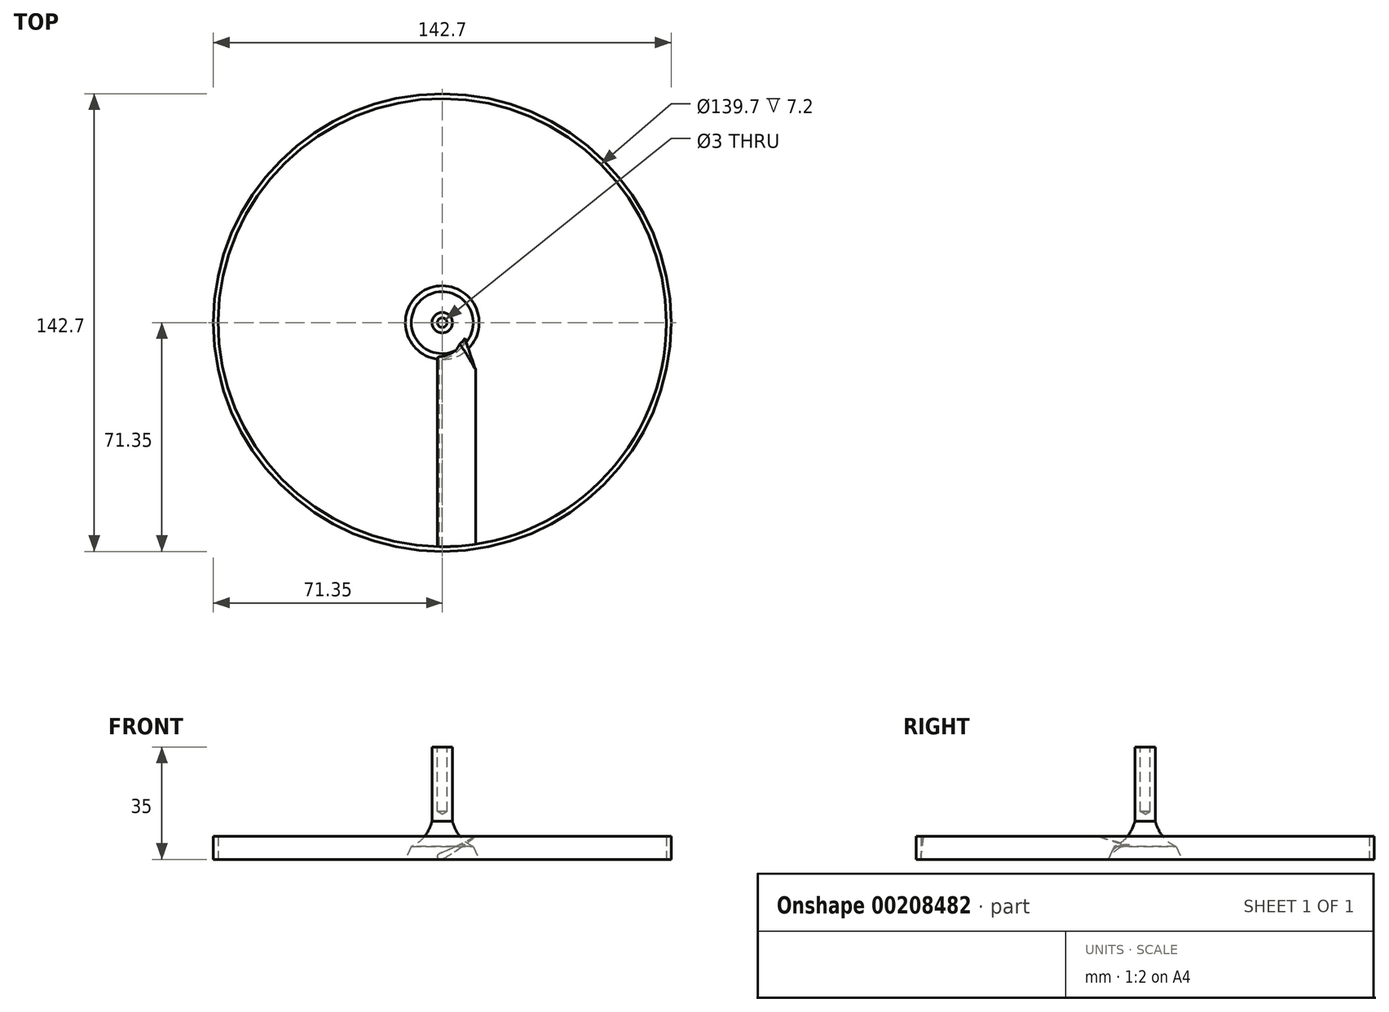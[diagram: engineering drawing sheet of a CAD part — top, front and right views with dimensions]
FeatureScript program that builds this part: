
annotation { "Feature Type Name" : "Feature", "Feature Type Description" : "" }
export const myFeature = defineFeature(function(context is Context, id is Id, definition is map)
    precondition{}
    {
        {
            var Q0;
            Q0=qCreatedBy(makeId("Front.planeOp"),FACE);
            var sketch = newSketch(context, id + "F0", { "sketchPlane" : qUnion([Q0])});
            skLineSegment(sketch, "E0", {"start": v(0, 0) * mm, "end": v(11, 6.35) * mm, "construction": true});
            skLineSegment(sketch, "E1", {"start": v(0, 0) * mm, "end": v(3.86, 0) * mm, "construction": true});
            skLineSegment(sketch, "E2.0", {"start": v(-0.62, 0.8) * mm, "end": v(10.38, 7.14) * mm, "construction": true});
            skFitSpline(sketch, "E3", {"points": [v(0, 0) * mm, v(2.62, 1.51) * mm, v(7.27, 4.68) * mm, v(10.38, 7.14) * mm], "startDerivative": vector(8.9, 4.4) * mm, "endDerivative": vector(8.82, 7.21) * mm});
            skLineSegment(sketch, "E4.0", {"start": v(-0.75, 1.88) * mm, "end": v(9.88, 8.01) * mm, "construction": true});
            skFitSpline(sketch, "E5", {"points": [v(-0.75, 1.88) * mm, v(2.33, 3.15) * mm, v(6.1, 4.85) * mm, v(10.38, 7.14) * mm], "startDerivative": vector(11.35, 3.56) * mm, "endDerivative": vector(12.14, 6.7) * mm});
            skArc(sketch, "E6", {"start": v(-0.75, 1.88) * mm, "mid": v(-1.39, 0.53) * mm, "end": v(0, 0) * mm});
            skLineSegment(sketch, "E7", {"start": v(0, 0) * mm, "end": v(0, 29.65) * mm, "construction": true});
            skSolve(sketch);
        }
        {
            var Q0;
            Q0 = qSketchRegion(id + "F0", true);
            extrude(context, id + "F1", {"entities" : qUnion([Q0]), "depth" : 69.85 * mm});
        }
        {
            var Q0;
            Q0=qCreatedBy(makeId("Front.planeOp"),FACE);
            var sketch = newSketch(context, id + "F2", { "sketchPlane" : qUnion([Q0])});
            skLineSegment(sketch, "E8", {"start": v(0, 2.13) * mm, "end": v(20.26, 7.8) * mm});
            skLineSegment(sketch, "E9", {"start": v(20.26, 7.8) * mm, "end": v(0, 7.8) * mm});
            skLineSegment(sketch, "E10", {"start": v(0, 7.8) * mm, "end": v(0, 2.13) * mm});
            skSolve(sketch);
        }
        {
            var Q0;
            Q0 = qSketchRegion(id + "F2", true);
            var Q1;
            Q1=sQuery(id+"F0.wireOp",EDGE,"E7");
            revolve(context, id + "F3", {"operationType" : NewBodyOperationType.REMOVE, "entities" : qUnion([Q0]), "axis" : qUnion([Q1]), "revolveType" : RevolveType.FULL, "oppositeDirection" : true});
        }
        {
            var Q0;
            Q0=qCreatedBy(makeId("Top.planeOp"),FACE);
            var sketch = newSketch(context, id + "F4", { "sketchPlane" : qUnion([Q0])});
            skCircle(sketch, "E11", {"center": v(0, 0) * mm, "radius": 3.18 * mm});
            skSolve(sketch);
        }
        {
            var Q0;
            Q0 = qSketchRegion(id + "F4", true);
            extrude(context, id + "F5", {"entities" : qUnion([Q0]), "operationType" : NewBodyOperationType.ADD, "depth" : 35 * mm});
        }
        {
            var Q0;
            Q0=qCreatedBy(makeId("Right.planeOp"),FACE);
            var sketch = newSketch(context, id + "F6", { "sketchPlane" : qUnion([Q0])});
            skLineSegment(sketch, "E12", {"start": v(0, 0) * mm, "end": v(-254, 0) * mm});
            skLineSegment(sketch, "E13.0", {"start": v(0, -23) * mm, "end": v(-254, -23) * mm});
            skLineSegment(sketch, "E14", {"start": v(-254, -23) * mm, "end": v(-254, 0) * mm});
            skLineSegment(sketch, "E15", {"start": v(0, -23) * mm, "end": v(0, 0) * mm});
            skSolve(sketch);
        }
        {
            var Q0;
            Q0 = qSketchRegion(id + "F6", true);
            var Q1;
            Q1 = qConstructionFilter(qBodyType(qCreatedBy(id + "F6" ,EDGE), BodyType.WIRE), ConstructionObject.NO);
            var Q2;
            Q2=sQuery(id+"F0.wireOp",EDGE,"E7");
            revolve(context, id + "F7", {"operationType" : NewBodyOperationType.REMOVE, "entities" : qUnion([Q0]), "surfaceEntities" : qUnion([Q1]), "axis" : qUnion([Q2]), "revolveType" : RevolveType.FULL});
        }
        {
            var Q0;
            Q0=qCreatedBy(makeId("Right.planeOp"),FACE);
            var sketch = newSketch(context, id + "F8", { "sketchPlane" : qUnion([Q0])});
            skLineSegment(sketch, "E16", {"start": v(-11.5, 0) * mm, "end": v(-1.5, 0) * mm});
            skLineSegment(sketch, "E17", {"start": v(-1.5, 0) * mm, "end": v(-1.5, 12.5) * mm});
            skLineSegment(sketch, "E18", {"start": v(-1.5, 12.5) * mm, "end": v(-3, 12.5) * mm});
            skFitSpline(sketch, "E19", {"points": [v(-3, 12.5) * mm, v(-4.7, 8.33) * mm, v(-6.96, 5.64) * mm, v(-9.65, 3.97) * mm], "startDerivative": vector(-3, -12.47) * mm, "endDerivative": vector(-9.37, -4.97) * mm});
            skLineSegment(sketch, "E20", {"start": v(-9.65, 3.97) * mm, "end": v(-11.5, 0) * mm});
            skSolve(sketch);
        }
        {
            var Q0;
            Q0 = qSketchRegion(id + "F8", true);
            var Q1;
            Q1=sQuery(id+"F0.wireOp",EDGE,"E7");
            revolve(context, id + "F9", {"operationType" : NewBodyOperationType.ADD, "entities" : qUnion([Q0]), "axis" : qUnion([Q1]), "revolveType" : RevolveType.FULL});
        }
        {
            var Q0;
            Q0=qCreatedBy(makeId("Top.planeOp"),FACE);
            var sketch = newSketch(context, id + "F10", { "sketchPlane" : qUnion([Q0])});
            skCircle(sketch, "E21", {"center": v(0, 0) * mm, "radius": 69.85 * mm});
            skCircle(sketch, "E22.0", {"center": v(0, 0) * mm, "radius": 71.35 * mm});
            skSolve(sketch);
        }
        {
            var Q0;
            Q0 = qSketchRegion(id + "F10", true);
            extrude(context, id + "F11", {"entities" : qUnion([Q0]), "operationType" : NewBodyOperationType.ADD, "depth" : 7.2 * mm});
        }
        {
            var Q0;
            Q0=makeQuery(id+"F5.opExtrude","CAP_FACE",FACE,{"disambiguationData":[OSD([sQuery(id+"F4.wireOp",EDGE,"E11")])],"isStart":false});
            var sketch = newSketch(context, id + "F12", { "sketchPlane" : qUnion([Q0])});
            skPoint(sketch, "E23", {"position": v(0, 0) * mm});
            skSolve(sketch);
        }
        {
            var Q0;
            Q0=sQuery(id+"F12.wireOp",VERTEX,"E23");
            var Q1;
            Q1=makeQuery(id+"F1.opExtrude","SWEPT_BODY",BODY,{"disambiguationData":[OSD([sQuery(id+"F0.wireOp",EDGE,"E3"),sQuery(id+"F0.wireOp",EDGE,"E5"),sQuery(id+"F0.wireOp",EDGE,"E6")])]});
            hole(context, id + "F13", {"style" : HoleStyle.SIMPLE, "endStyle" : HoleEndStyle.BLIND, "holeDiameter" : 3 * mm, "holeDepth" : 20 * mm, "locations" : qUnion([Q0]), "scope" : qUnion([Q1])});
        }
    });
